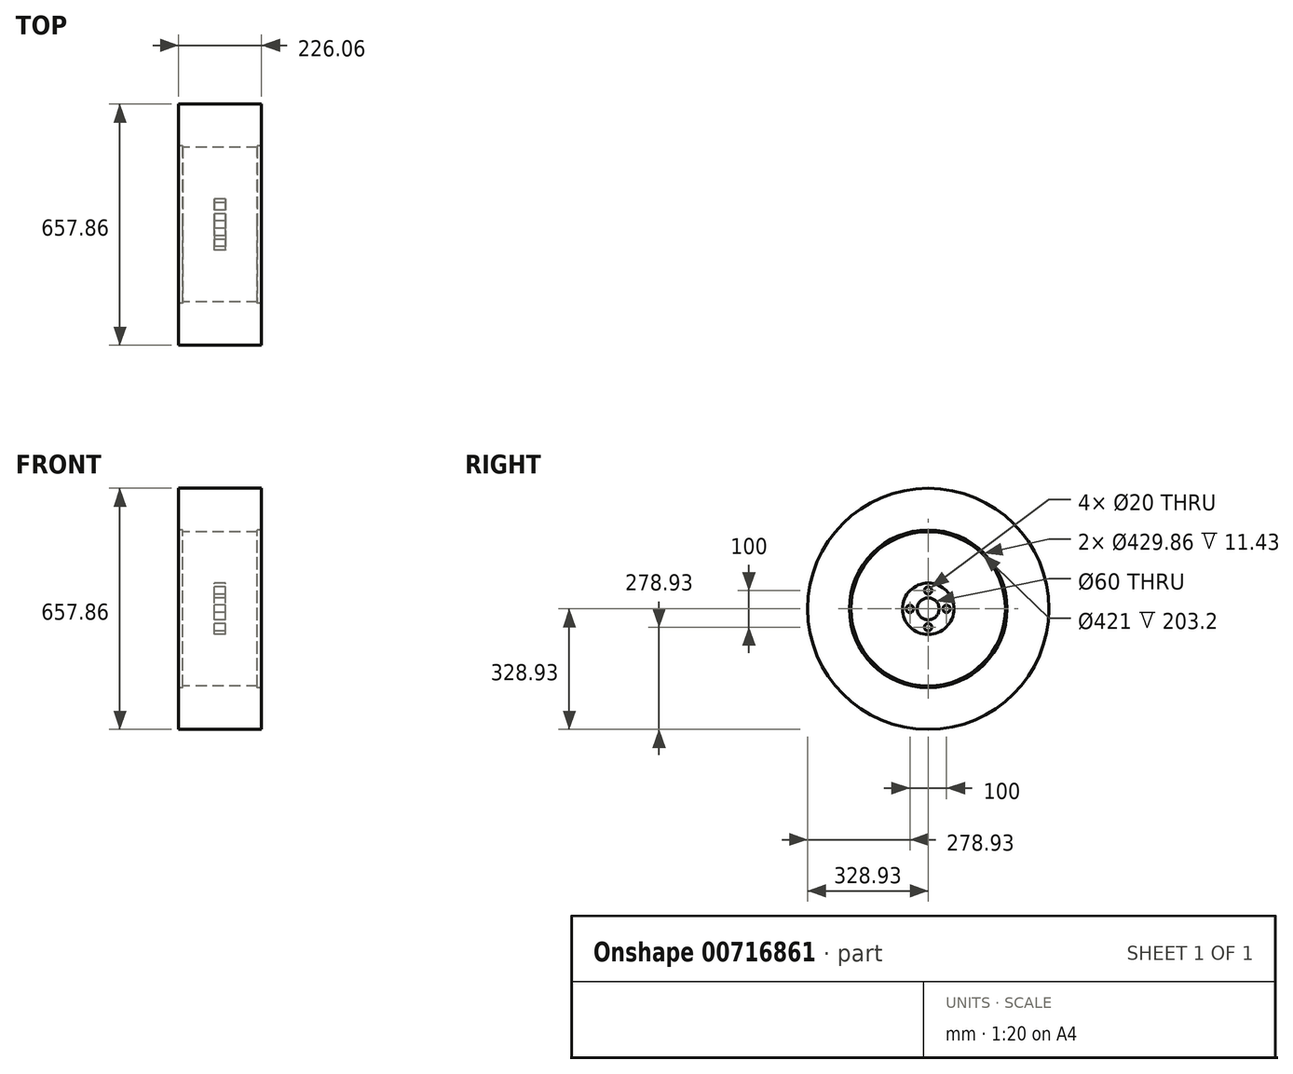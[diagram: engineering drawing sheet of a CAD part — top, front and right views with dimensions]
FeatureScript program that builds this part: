
annotation { "Feature Type Name" : "Feature", "Feature Type Description" : "" }
export const myFeature = defineFeature(function(context is Context, id is Id, definition is map)
    precondition{}
    {
        {
            var Q0;
            Q0=qCreatedBy(makeId("Right.planeOp"),FACE);
            var sketch = newSketch(context, id + "F0", { "sketchPlane" : qUnion([Q0])});
            skCircle(sketch, "E0", {"center": v(0, 0) * mm, "radius": 215.5 * mm});
            skCircle(sketch, "E1", {"center": v(0, 0) * mm, "radius": 210.5 * mm});
            skSolve(sketch);
        }
        {
            var Q0;
            Q0=makeQuery(id+"F0.imprint","IMPRINT",FACE,{"disambiguationData":[TD([[makeQuery(id+"F0.imprint","IMPRINT",EDGE,{"derivedFrom":sQuery(id+"F0.wireOp",EDGE,"E0")}),1.0]])]});
            extrude(context, id + "F1", {"entities" : qUnion([Q0]), "endBound" : BoundingType.SYMMETRIC, "depth" : 203.2 * mm, "offsetDistance" : 25 * mm});
        }
        {
            var Q0;
            Q0=qCreatedBy(makeId("Right.planeOp"),FACE);
            var sketch = newSketch(context, id + "F2", { "sketchPlane" : qUnion([Q0])});
            skCircle(sketch, "E2", {"center": v(0, 0) * mm, "radius": 30 * mm});
            skCircle(sketch, "E3", {"center": v(0, 50) * mm, "radius": 10 * mm});
            skCircle(sketch, "E4", {"center": v(50, 0) * mm, "radius": 10 * mm});
            skCircle(sketch, "E5", {"center": v(0, -50) * mm, "radius": 10 * mm});
            skCircle(sketch, "E6", {"center": v(-50, 0) * mm, "radius": 10 * mm});
            skCircle(sketch, "E7", {"center": v(0, 0) * mm, "radius": 70 * mm});
            skSolve(sketch);
        }
        {
            var Q0;
            Q0 = qSketchRegion(id + "F2", true);
            extrude(context, id + "F3", {"entities" : qUnion([Q0]), "endBound" : BoundingType.SYMMETRIC, "depth" : 30 * mm, "offsetDistance" : 25 * mm});
        }
        {
            var Q0;
            Q0=qCreatedBy(makeId("Right.planeOp"),FACE);
            var sketch = newSketch(context, id + "F4", { "sketchPlane" : qUnion([Q0])});
            skCircle(sketch, "E8", {"center": v(0, 0) * mm, "radius": 328.93 * mm});
            skCircle(sketch, "E9.0", {"center": v(0, 0) * mm, "radius": 214.93 * mm});
            skSolve(sketch);
        }
        {
            var Q0;
            Q0=makeQuery(id+"F4.imprint","IMPRINT",FACE,{"disambiguationData":[TD([[makeQuery(id+"F4.imprint","IMPRINT",EDGE,{"derivedFrom":sQuery(id+"F4.wireOp",EDGE,"E8")}),1.0]])]});
            extrude(context, id + "F5", {"entities" : qUnion([Q0]), "operationType" : NewBodyOperationType.ADD, "endBound" : BoundingType.SYMMETRIC, "depth" : 226.06 * mm, "offsetDistance" : 25 * mm});
        }
    });
